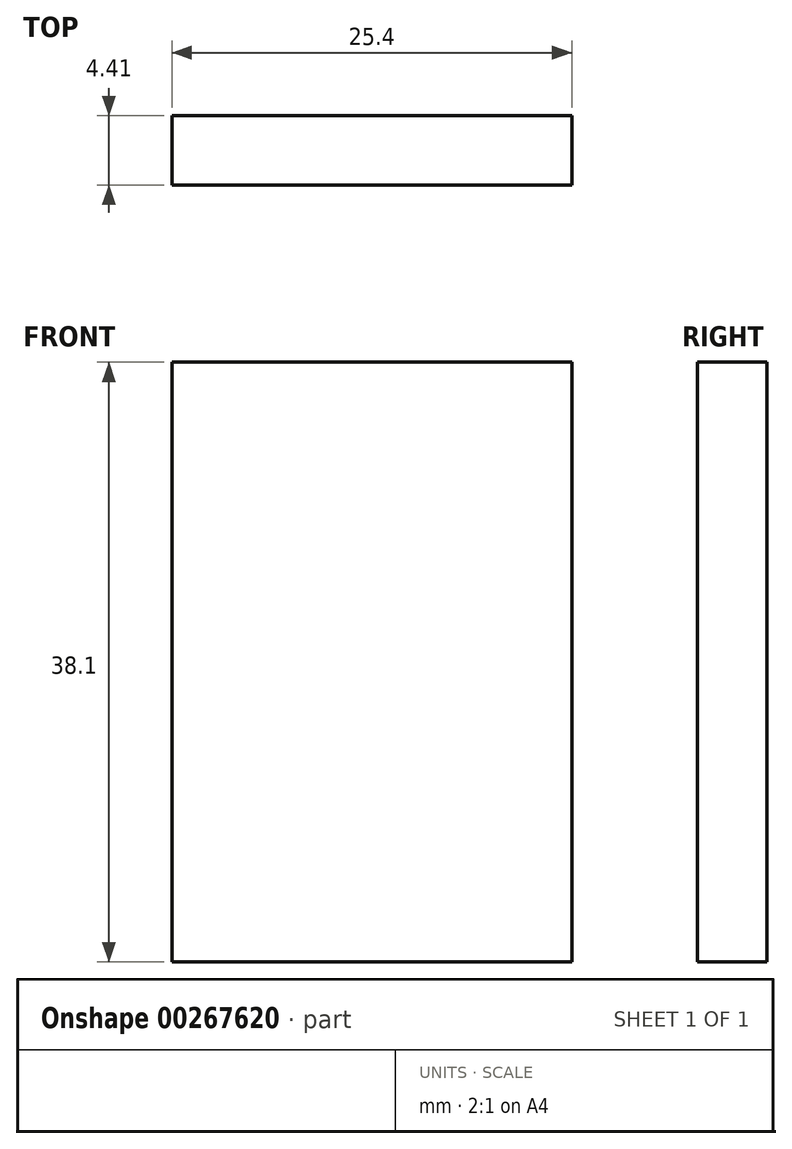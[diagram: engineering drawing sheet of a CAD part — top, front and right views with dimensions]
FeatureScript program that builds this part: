
annotation { "Feature Type Name" : "Feature", "Feature Type Description" : "" }
export const myFeature = defineFeature(function(context is Context, id is Id, definition is map)
    precondition{}
    {
        {
            var Q0;
            Q0=qCreatedBy(makeId("Front.planeOp"),FACE);
            var sketch = newSketch(context, id + "F0", { "sketchPlane" : qUnion([Q0])});
            skLineSegment(sketch, "E0.bottom", {"start": v(12.7, 19.05) * mm, "end": v(-12.7, 19.05) * mm});
            skLineSegment(sketch, "E0.top", {"start": v(12.7, -19.05) * mm, "end": v(-12.7, -19.05) * mm});
            skLineSegment(sketch, "E0.left", {"start": v(12.7, 19.05) * mm, "end": v(12.7, -19.05) * mm});
            skLineSegment(sketch, "E0.right", {"start": v(-12.7, 19.05) * mm, "end": v(-12.7, -19.05) * mm});
            skPoint(sketch, "E0.middle", {"position": v(0, 0) * mm});
            skSolve(sketch);
        }
        {
            var Q0;
            Q0 = qSketchRegion(id + "F0", true);
            extrude(context, id + "F1", {"entities" : qUnion([Q0]), "depth" : 4.4 * mm});
        }
    });
